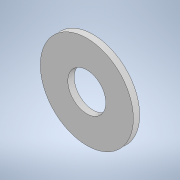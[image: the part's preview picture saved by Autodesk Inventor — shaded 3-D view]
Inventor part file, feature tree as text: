
AUTODESK INVENTOR PART (.ipt)
format: ipt  version: 2021 (Build 250183000, 183)  size: 96,768 bytes
history: native  units: mm
features: extrude x1, sketch x1
ambient origin geometry x8: Origin, YZ Plane, XZ Plane, XY Plane, X Axis, Y Axis, Z Axis, Center Point
bodies: Solid1 (feature_tree)
feature tree (2):
  extrude  "Extrusion1"  Depth=1.5mm
  sketch  "Sketch1"  dims[d0=9.0mm d1=22.0mm d2=1.5mm d3=0.0mm]
